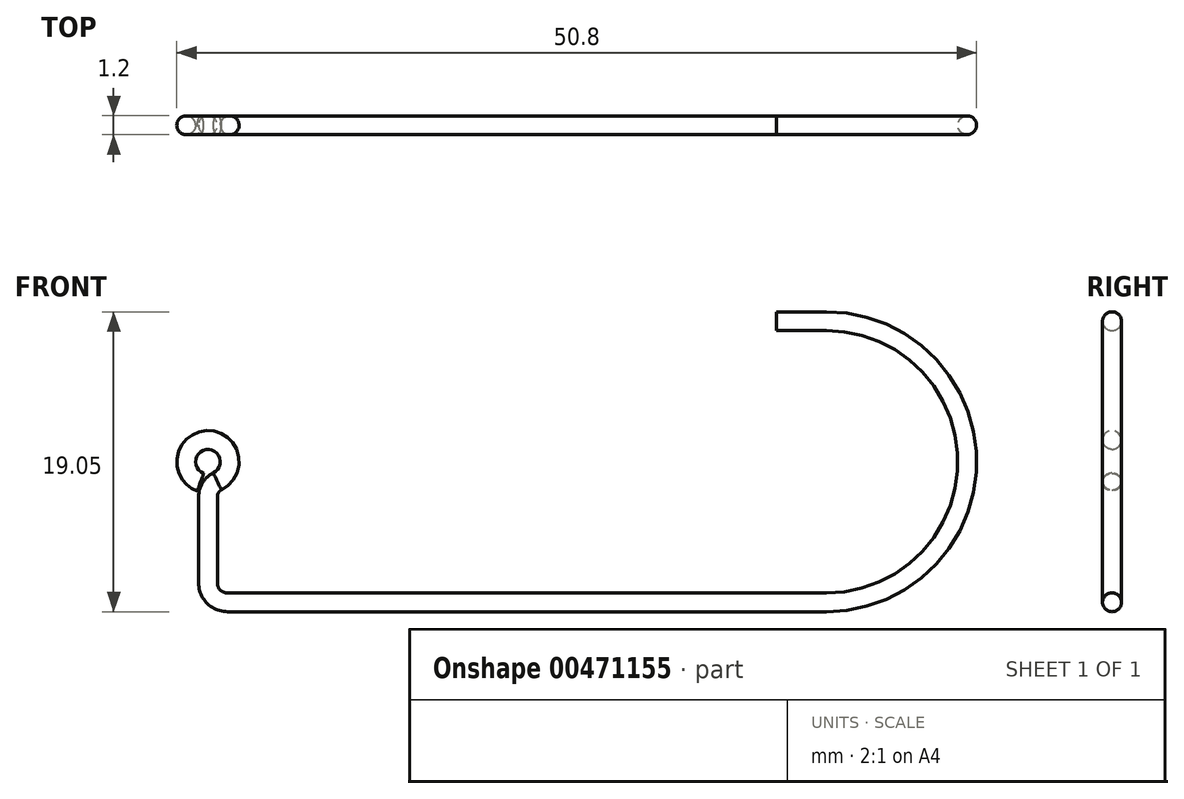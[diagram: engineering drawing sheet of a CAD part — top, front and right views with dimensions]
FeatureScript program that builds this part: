
annotation { "Feature Type Name" : "Feature", "Feature Type Description" : "" }
export const myFeature = defineFeature(function(context is Context, id is Id, definition is map)
    precondition{}
    {
        {
            var Q0;
            Q0=qCreatedBy(makeId("Front.planeOp"),FACE);
            var sketch = newSketch(context, id + "F0", { "sketchPlane" : qUnion([Q0])});
            skLineSegment(sketch, "E0.bottom", {"start": v(2.65, 0) * mm, "end": v(41.28, 0) * mm});
            skLineSegment(sketch, "E0.top", {"start": v(38.1, 19.05) * mm, "end": v(41.28, 19.05) * mm});
            skLineSegment(sketch, "E0.right", {"start": v(50.8, 9.53) * mm, "end": v(50.8, 9.52) * mm});
            skArc(sketch, "E1.filletArc", {"start": v(50.8, 9.52) * mm, "mid": v(48.01, 16.26) * mm, "end": v(41.28, 19.05) * mm});
            skArc(sketch, "E2.filletArc", {"start": v(41.28, 0) * mm, "mid": v(48.01, 2.79) * mm, "end": v(50.8, 9.53) * mm});
            skLineSegment(sketch, "E3", {"start": v(3.21, 1.2) * mm, "end": v(41.28, 1.2) * mm});
            skArc(sketch, "E4", {"start": v(41.28, 1.2) * mm, "mid": v(49.6, 9.53) * mm, "end": v(41.28, 17.86) * mm});
            skLineSegment(sketch, "E5", {"start": v(39.67, 16.69) * mm, "end": v(38.1, 17.86) * mm});
            skLineSegment(sketch, "E6", {"start": v(41.28, 17.86) * mm, "end": v(40.06, 17.86) * mm});
            skLineSegment(sketch, "E7", {"start": v(38.56, 18.03) * mm, "end": v(40.06, 17.86) * mm});
            skArc(sketch, "E8", {"start": v(38.1, 19.05) * mm, "mid": v(34.91, 18.9) * mm, "end": v(31.75, 18.45) * mm});
            skArc(sketch, "E9", {"start": v(2.33, 8.8) * mm, "mid": v(1.94, 10.32) * mm, "end": v(1.7, 8.77) * mm});
            skArc(sketch, "E10", {"start": v(2.84, 7.74) * mm, "mid": v(1.89, 11.5) * mm, "end": v(1.3, 7.67) * mm});
            skLineSegment(sketch, "E11", {"start": v(2.58, 7.3) * mm, "end": v(2.58, 1.83) * mm});
            skLineSegment(sketch, "E12", {"start": v(1.38, 7.3) * mm, "end": v(1.38, 1.27) * mm});
            skPoint(sketch, "E13.orphan", {"position": v(0, 9.53) * mm});
            skArc(sketch, "E14.filletArc", {"start": v(2.58, 1.83) * mm, "mid": v(2.76, 1.38) * mm, "end": v(3.21, 1.2) * mm});
            skPoint(sketch, "E15.visualSharp", {"position": v(1.38, 0) * mm});
            skArc(sketch, "E15.filletArc", {"start": v(1.38, 1.27) * mm, "mid": v(1.76, 0.37) * mm, "end": v(2.65, 0) * mm});
            skLineSegment(sketch, "E16", {"start": v(41.28, 1.2) * mm, "end": v(41.28, 0) * mm});
            skLineSegment(sketch, "E17", {"start": v(41.28, 1.2) * mm, "end": v(41.28, 0.6) * mm});
            skLineSegment(sketch, "E18", {"start": v(1.7, 8.77) * mm, "end": v(1.5, 8.22) * mm});
            skLineSegment(sketch, "E19", {"start": v(1.5, 8.22) * mm, "end": v(1.3, 7.67) * mm});
            skLineSegment(sketch, "E20", {"start": v(1.98, 7.3) * mm, "end": v(2.58, 7.3) * mm});
            skLineSegment(sketch, "E21", {"start": v(1.98, 7.3) * mm, "end": v(1.98, 7.17) * mm});
            skArc(sketch, "E22", {"start": v(2.84, 7.74) * mm, "mid": v(2.65, 7.56) * mm, "end": v(2.58, 7.3) * mm});
            skLineSegment(sketch, "E23", {"start": v(38.1, 18.45) * mm, "end": v(37.57, 18.45) * mm});
            skLineSegment(sketch, "E24", {"start": v(38.1, 17.86) * mm, "end": v(40.06, 17.86) * mm});
            skSolve(sketch);
        }
        {
            var Q0;
            Q0=sQuery(id+"F0.wireOp",EDGE,"E20");
            var Q1;
            Q1=sQuery(id+"F0.wireOp",EDGE,"E21");
            revolve(context, id + "F1", {"bodyType" : ToolBodyType.SURFACE, "surfaceEntities" : qUnion([Q0]), "axis" : qUnion([Q1]), "revolveType" : RevolveType.FULL});
        }
        {
            var Q0;
            Q0=makeQuery(id+"F1.opRevolve","SWEPT_FACE",FACE,{"disambiguationData":[OSD([sQuery(id+"F0.wireOp",EDGE,"E20")])]});
            var Q1;
            Q1=sQuery(id+"F0.wireOp",EDGE,"E22");
            var Q2;
            Q2=sQuery(id+"F0.wireOp",EDGE,"E10");
            sweep(context, id + "F2", {"profiles" : qUnion([Q0]), "path" : qUnion([Q1, Q2])});
        }
        {
            var Q0;
            Q0=makeQuery(id+"F1.opRevolve","SWEPT_FACE",FACE,{"disambiguationData":[OSD([sQuery(id+"F0.wireOp",EDGE,"E20")])]});
            var Q1;
            Q1=sQuery(id+"F0.wireOp",EDGE,"E11");
            var Q2;
            Q2=sQuery(id+"F0.wireOp",EDGE,"E14.filletArc");
            var Q3;
            Q3=sQuery(id+"F0.wireOp",EDGE,"E3");
            var Q4;
            Q4=sQuery(id+"F0.wireOp",EDGE,"E4");
            sweep(context, id + "F3", {"operationType" : NewBodyOperationType.ADD, "profiles" : qUnion([Q0]), "path" : qUnion([Q1, Q2, Q3, Q4])});
        }
        {
            var Q0;
            Q0=sQuery(id+"F0.wireOp",EDGE,"E8");
            var Q1;
            Q1=sQuery(id+"F0.wireOp",EDGE,"E23");
            revolve(context, id + "F4", {"bodyType" : ToolBodyType.SURFACE, "surfaceEntities" : qUnion([Q0]), "axis" : qUnion([Q1]), "revolveType" : RevolveType.FULL});
        }
        {
            var Q0;
            Q0=makeQuery(id+"F3.opSweep","CAP_FACE",FACE,{"disambiguationData":[OSD([sQuery(id+"F0.wireOp",VERTEX,"E4.end"),sQuery(id+"F0.wireOp",EDGE,"E20")])],"isStart":false});
            var Q1;
            Q1=sQuery(id+"F0.wireOp",EDGE,"E0.top");
            sweep(context, id + "F5", {"operationType" : NewBodyOperationType.ADD, "profiles" : qUnion([Q0]), "path" : qUnion([Q1])});
        }
    });
